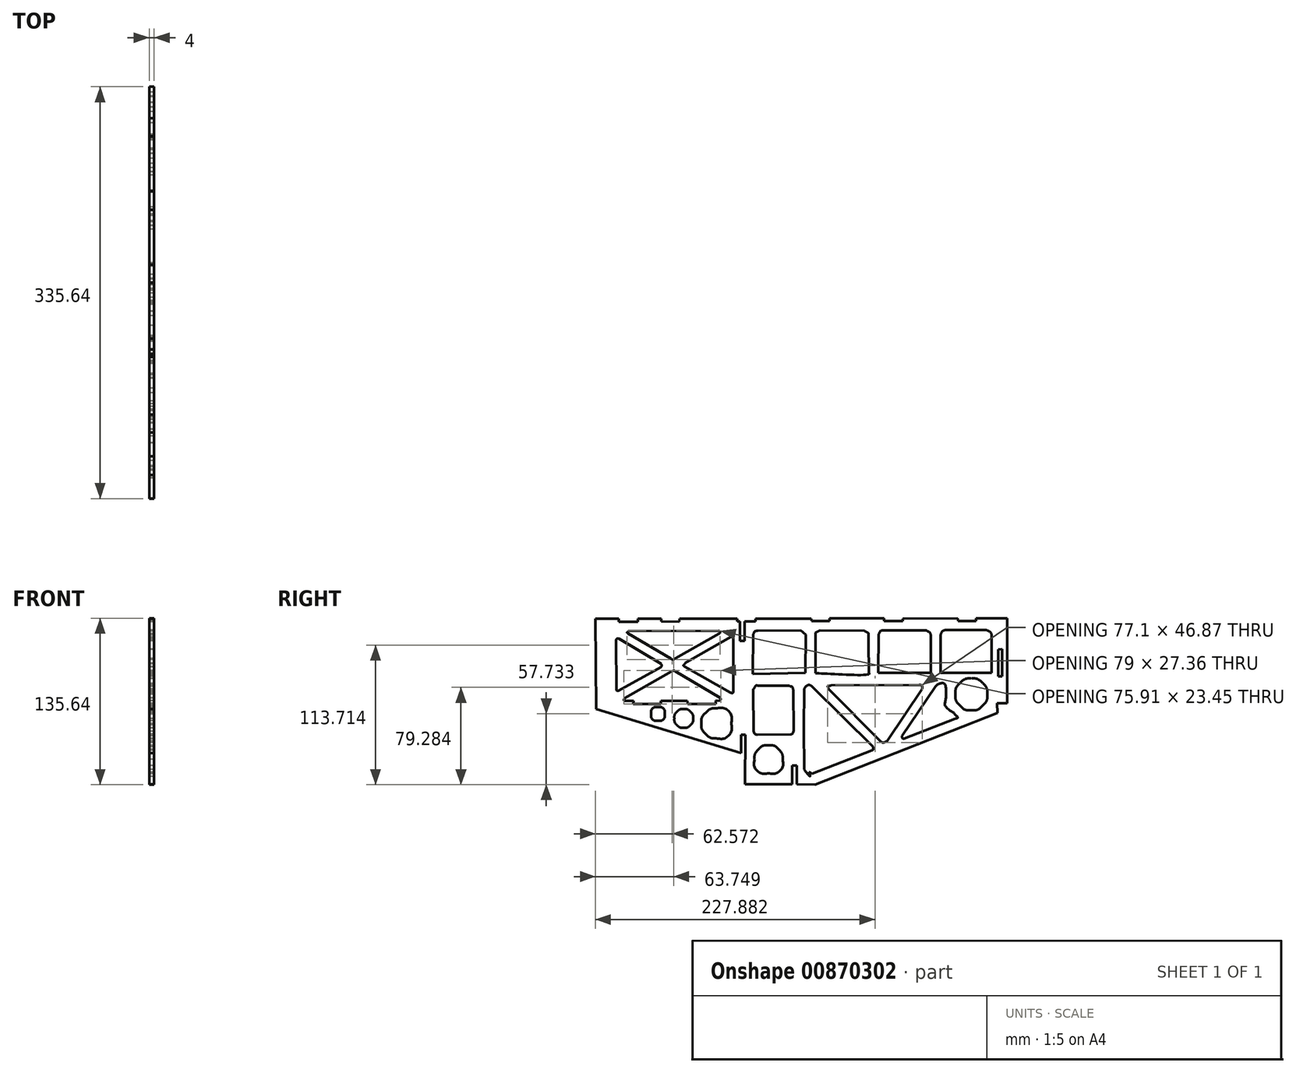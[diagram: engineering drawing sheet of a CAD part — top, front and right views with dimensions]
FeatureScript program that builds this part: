
annotation { "Feature Type Name" : "Feature", "Feature Type Description" : "" }
export const myFeature = defineFeature(function(context is Context, id is Id, definition is map)
    precondition{}
    {
        {
            var Q0;
            Q0=qCreatedBy(makeId("Right.planeOp"),FACE);
            var sketch = newSketch(context, id + "F0", { "sketchPlane" : qUnion([Q0])});
            skLineSegment(sketch, "E0", {"start": v(-35.34, 12.8) * mm, "end": v(-9.65, 12.66) * mm});
            skLineSegment(sketch, "E1", {"start": v(-6.53, 9.34) * mm, "end": v(-6.37, -24.32) * mm});
            skLineSegment(sketch, "E2", {"start": v(-8.68, -26.77) * mm, "end": v(-36.17, -27.13) * mm});
            skLineSegment(sketch, "E3", {"start": v(-38.88, -24.36) * mm, "end": v(-39.35, 9.67) * mm});
            skLineSegment(sketch, "E4", {"start": v(-167.82, 67.26) * mm, "end": v(-148.64, 67.36) * mm});
            skLineSegment(sketch, "E5", {"start": v(-148.64, 67.36) * mm, "end": v(-148.66, 64.78) * mm});
            skLineSegment(sketch, "E6", {"start": v(-148.66, 64.78) * mm, "end": v(-133.38, 64.95) * mm});
            skLineSegment(sketch, "E7", {"start": v(-133.38, 64.95) * mm, "end": v(-133.35, 67.39) * mm});
            skLineSegment(sketch, "E8", {"start": v(-133.35, 67.39) * mm, "end": v(-114.03, 67.41) * mm});
            skLineSegment(sketch, "E9", {"start": v(-114.03, 67.41) * mm, "end": v(-114.18, 65.04) * mm});
            skLineSegment(sketch, "E10", {"start": v(-114.18, 65.04) * mm, "end": v(-99.45, 65) * mm});
            skLineSegment(sketch, "E11", {"start": v(-99.45, 65) * mm, "end": v(-99.35, 67.43) * mm});
            skLineSegment(sketch, "E12", {"start": v(-99.35, 67.43) * mm, "end": v(-52.32, 67.5) * mm});
            skLineSegment(sketch, "E13", {"start": v(-52.32, 67.5) * mm, "end": v(-52.32, 65.13) * mm});
            skLineSegment(sketch, "E14", {"start": v(-52.32, 65.13) * mm, "end": v(-50.06, 65.16) * mm});
            skLineSegment(sketch, "E15", {"start": v(-50.06, 65.16) * mm, "end": v(-50.04, 49.2) * mm});
            skLineSegment(sketch, "E16", {"start": v(-50.04, 49.2) * mm, "end": v(-46.26, 49.2) * mm});
            skLineSegment(sketch, "E17", {"start": v(-46.26, 49.2) * mm, "end": v(-46.26, 65.21) * mm});
            skLineSegment(sketch, "E18", {"start": v(-46.26, 65.21) * mm, "end": v(-37.38, 65.34) * mm});
            skLineSegment(sketch, "E19", {"start": v(-37.38, 65.34) * mm, "end": v(-37.43, 67.48) * mm});
            skLineSegment(sketch, "E20", {"start": v(-37.43, 67.48) * mm, "end": v(8.06, 67.55) * mm});
            skLineSegment(sketch, "E21", {"start": v(8.06, 67.55) * mm, "end": v(8.26, 65.47) * mm});
            skLineSegment(sketch, "E22", {"start": v(8.26, 65.47) * mm, "end": v(22.9, 65.44) * mm});
            skLineSegment(sketch, "E23", {"start": v(22.9, 65.44) * mm, "end": v(23, 67.58) * mm});
            skLineSegment(sketch, "E24", {"start": v(23, 67.58) * mm, "end": v(67.49, 67.65) * mm});
            skLineSegment(sketch, "E25", {"start": v(67.49, 67.65) * mm, "end": v(67.44, 65.38) * mm});
            skLineSegment(sketch, "E26", {"start": v(67.44, 65.38) * mm, "end": v(82.72, 65.5) * mm});
            skLineSegment(sketch, "E27", {"start": v(82.72, 65.5) * mm, "end": v(82.82, 67.53) * mm});
            skLineSegment(sketch, "E28", {"start": v(82.82, 67.53) * mm, "end": v(127.42, 67.68) * mm});
            skLineSegment(sketch, "E29", {"start": v(127.42, 67.68) * mm, "end": v(127.62, 65.56) * mm});
            skLineSegment(sketch, "E30", {"start": v(127.62, 65.56) * mm, "end": v(142.25, 65.54) * mm});
            skLineSegment(sketch, "E31", {"start": v(142.25, 65.54) * mm, "end": v(142.3, 67.74) * mm});
            skLineSegment(sketch, "E32", {"start": v(142.3, 67.74) * mm, "end": v(167.82, 67.82) * mm});
            skLineSegment(sketch, "E33", {"start": v(167.82, 67.82) * mm, "end": v(167.82, -1.63) * mm});
            skLineSegment(sketch, "E34", {"start": v(167.82, -1.63) * mm, "end": v(159.6, -1.35) * mm});
            skLineSegment(sketch, "E35", {"start": v(159.6, -1.35) * mm, "end": v(159.88, -9.57) * mm});
            skLineSegment(sketch, "E36", {"start": v(159.88, -9.57) * mm, "end": v(11.27, -67.82) * mm});
            skLineSegment(sketch, "E37", {"start": v(11.27, -67.82) * mm, "end": v(-3.77, -67.68) * mm});
            skLineSegment(sketch, "E38", {"start": v(-3.77, -67.68) * mm, "end": v(-3.76, -52.35) * mm});
            skLineSegment(sketch, "E39", {"start": v(-3.76, -52.35) * mm, "end": v(-7.49, -52.33) * mm});
            skLineSegment(sketch, "E40", {"start": v(-7.49, -52.33) * mm, "end": v(-7.63, -67.6) * mm});
            skLineSegment(sketch, "E41", {"start": v(-7.63, -67.6) * mm, "end": v(-45.92, -67.68) * mm});
            skLineSegment(sketch, "E42", {"start": v(-45.92, -67.68) * mm, "end": v(-45.64, -27.14) * mm});
            skLineSegment(sketch, "E43", {"start": v(-45.64, -27.14) * mm, "end": v(-49.04, -27.14) * mm});
            skLineSegment(sketch, "E44", {"start": v(-49.04, -27.14) * mm, "end": v(-49.04, -42.17) * mm});
            skLineSegment(sketch, "E45", {"start": v(-49.04, -42.17) * mm, "end": v(-167.25, -6.17) * mm});
            skLineSegment(sketch, "E46", {"start": v(-167.25, -6.17) * mm, "end": v(-167.82, 67.26) * mm});
            skLineSegment(sketch, "E47", {"start": v(-140.96, 57.3) * mm, "end": v(-67.1, 57.62) * mm});
            skLineSegment(sketch, "E48", {"start": v(-66.89, 55.38) * mm, "end": v(-102.87, 34.97) * mm});
            skLineSegment(sketch, "E49", {"start": v(-106.46, 34.95) * mm, "end": v(-141.33, 55.29) * mm});
            skLineSegment(sketch, "E50", {"start": v(-140.96, 57.3) * mm, "end": v(-140.96, 57.3) * mm});
            skLineSegment(sketch, "E51", {"start": v(-94.85, 31.14) * mm, "end": v(-57.55, 52.48) * mm});
            skLineSegment(sketch, "E52", {"start": v(-55.38, 51.31) * mm, "end": v(-55.44, 8.2) * mm});
            skLineSegment(sketch, "E53", {"start": v(-57.81, 6.93) * mm, "end": v(-95.2, 28.46) * mm});
            skLineSegment(sketch, "E54", {"start": v(-102.8, 24.6) * mm, "end": v(-66.15, 2.96) * mm});
            skLineSegment(sketch, "E55", {"start": v(-67.02, 0.55) * mm, "end": v(-69.9, 0.58) * mm});
            skLineSegment(sketch, "E56", {"start": v(-69.9, 0.58) * mm, "end": v(-69.86, -2.02) * mm});
            skLineSegment(sketch, "E57", {"start": v(-69.86, -2.02) * mm, "end": v(-92.66, -2.05) * mm});
            skLineSegment(sketch, "E58", {"start": v(-92.66, -2.05) * mm, "end": v(-92.83, 0.56) * mm});
            skLineSegment(sketch, "E59", {"start": v(-92.83, 0.56) * mm, "end": v(-114.44, 0.44) * mm});
            skLineSegment(sketch, "E60", {"start": v(-114.44, 0.44) * mm, "end": v(-114.48, -2.15) * mm});
            skLineSegment(sketch, "E61", {"start": v(-114.48, -2.15) * mm, "end": v(-136.93, -2.21) * mm});
            skLineSegment(sketch, "E62", {"start": v(-136.93, -2.21) * mm, "end": v(-136.82, 0.35) * mm});
            skLineSegment(sketch, "E63", {"start": v(-136.82, 0.35) * mm, "end": v(-143.8, 0.35) * mm});
            skLineSegment(sketch, "E64", {"start": v(-144.07, 2.52) * mm, "end": v(-105.61, 24.62) * mm});
            skLineSegment(sketch, "E65", {"start": v(-102.8, 24.6) * mm, "end": v(-102.8, 24.6) * mm});
            skLineSegment(sketch, "E66", {"start": v(-151.08, 49.68) * mm, "end": v(-150.86, 9.73) * mm});
            skLineSegment(sketch, "E67", {"start": v(-148.95, 8.56) * mm, "end": v(-114.29, 28.13) * mm});
            skLineSegment(sketch, "E68", {"start": v(-114.32, 30.7) * mm, "end": v(-148.8, 51.1) * mm});
            skLineSegment(sketch, "E69", {"start": v(-39.68, 22.48) * mm, "end": v(3.4, 23.32) * mm});
            skLineSegment(sketch, "E70", {"start": v(3.4, 23.32) * mm, "end": v(3.62, 54.46) * mm});
            skLineSegment(sketch, "E71", {"start": v(3.62, 54.46) * mm, "end": v(-0.4, 57.86) * mm});
            skLineSegment(sketch, "E72", {"start": v(-0.4, 57.86) * mm, "end": v(-35.54, 57.55) * mm});
            skLineSegment(sketch, "E73", {"start": v(-39.16, 54.7) * mm, "end": v(-39.68, 22.48) * mm});
            skLineSegment(sketch, "E74", {"start": v(11.5, 54.63) * mm, "end": v(11.63, 23.04) * mm});
            skLineSegment(sketch, "E75", {"start": v(51.66, 57.5) * mm, "end": v(15.06, 57.76) * mm});
            skLineSegment(sketch, "E76", {"start": v(62.96, 54.57) * mm, "end": v(62.8, 23.32) * mm});
            skLineSegment(sketch, "E77", {"start": v(62.8, 23.32) * mm, "end": v(105.38, 23.4) * mm});
            skLineSegment(sketch, "E78", {"start": v(105.38, 23.4) * mm, "end": v(105.49, 53.98) * mm});
            skLineSegment(sketch, "E79", {"start": v(102.03, 57.82) * mm, "end": v(66.65, 57.83) * mm});
            skLineSegment(sketch, "E80", {"start": v(117, 58.05) * mm, "end": v(151.01, 58.04) * mm});
            skLineSegment(sketch, "E81", {"start": v(155, 54.07) * mm, "end": v(155.21, 23.25) * mm});
            skLineSegment(sketch, "E82", {"start": v(155.21, 23.25) * mm, "end": v(113.4, 23.25) * mm});
            skLineSegment(sketch, "E83", {"start": v(113.4, 23.25) * mm, "end": v(113.6, 54.45) * mm});
            skLineSegment(sketch, "E84", {"start": v(109.43, 12.3) * mm, "end": v(82.13, -28.04) * mm});
            skLineSegment(sketch, "E85", {"start": v(83.67, -30.34) * mm, "end": v(125.16, -14.2) * mm});
            skLineSegment(sketch, "E86", {"start": v(160.44, 42.32) * mm, "end": v(163.63, 42.53) * mm});
            skLineSegment(sketch, "E87", {"start": v(163.63, 42.53) * mm, "end": v(163.5, 20.27) * mm});
            skLineSegment(sketch, "E88", {"start": v(163.5, 20.27) * mm, "end": v(160.45, 20.33) * mm});
            skLineSegment(sketch, "E89", {"start": v(160.45, 20.33) * mm, "end": v(160.44, 42.32) * mm});
            skLineSegment(sketch, "E90", {"start": v(24.48, 13.03) * mm, "end": v(95.92, 13.32) * mm});
            skLineSegment(sketch, "E91", {"start": v(98.38, 10.3) * mm, "end": v(69.94, -32.3) * mm});
            skLineSegment(sketch, "E92", {"start": v(64.18, -32.25) * mm, "end": v(22.67, 9.59) * mm});
            skLineSegment(sketch, "E93", {"start": v(8.6, 12.2) * mm, "end": v(58.54, -37.15) * mm});
            skLineSegment(sketch, "E94", {"start": v(57.67, -40.01) * mm, "end": v(8.58, -59.05) * mm});
            skLineSegment(sketch, "E95", {"start": v(2.21, -55.54) * mm, "end": v(1.94, -21.7) * mm});
            skLineSegment(sketch, "E96", {"start": v(1.94, -21.7) * mm, "end": v(2.26, 9.95) * mm});
            skFitSpline(sketch, "E97", {"points": [v(-9.65, 12.66) * mm, v(-8.65, 12.04) * mm, v(-7.7, 12.08) * mm, v(-6.53, 9.34) * mm]});
            skFitSpline(sketch, "E98", {"points": [v(-6.37, -24.32) * mm, v(-6.77, -25.51) * mm, v(-7.39, -26.52) * mm, v(-8.68, -26.77) * mm]});
            skFitSpline(sketch, "E99", {"points": [v(-36.17, -27.13) * mm, v(-37.8, -26.6) * mm, v(-38.46, -25.54) * mm, v(-38.88, -24.36) * mm]});
            skFitSpline(sketch, "E100", {"points": [v(-39.35, 9.67) * mm, v(-38.18, 11.2) * mm, v(-37.05, 12.9) * mm, v(-35.34, 12.8) * mm]});
            skFitSpline(sketch, "E101", {"points": [v(-67.1, 57.62) * mm, v(-66.58, 56.92) * mm, v(-66.12, 56.21) * mm, v(-66.89, 55.38) * mm]});
            skFitSpline(sketch, "E102", {"points": [v(-102.87, 34.97) * mm, v(-103.76, 34.34) * mm, v(-105.56, 34.27) * mm, v(-106.46, 34.95) * mm]});
            skFitSpline(sketch, "E103", {"points": [v(-141.33, 55.29) * mm, v(-142.03, 56.2) * mm, v(-141.57, 56.78) * mm, v(-140.96, 57.3) * mm]});
            skFitSpline(sketch, "E104", {"points": [v(-95.2, 28.46) * mm, v(-96.1, 29.46) * mm, v(-95.1, 30.4) * mm, v(-94.85, 31.14) * mm]});
            skFitSpline(sketch, "E105", {"points": [v(-57.55, 52.48) * mm, v(-56.71, 52.35) * mm, v(-55.72, 52.56) * mm, v(-55.38, 51.31) * mm]});
            skFitSpline(sketch, "E106", {"points": [v(-55.44, 8.2) * mm, v(-55.96, 6.75) * mm, v(-56.92, 6.9) * mm, v(-57.81, 6.93) * mm]});
            skFitSpline(sketch, "E107", {"points": [v(-66.15, 2.96) * mm, v(-65.76, 1.6) * mm, v(-66.3, 1) * mm, v(-67.02, 0.55) * mm]});
            skFitSpline(sketch, "E108", {"points": [v(-143.8, 0.35) * mm, v(-144.74, 1.02) * mm, v(-144.5, 1.76) * mm, v(-144.07, 2.52) * mm]});
            skFitSpline(sketch, "E109", {"points": [v(-105.61, 24.62) * mm, v(-104.72, 24.84) * mm, v(-103.83, 25.14) * mm, v(-102.8, 24.6) * mm]});
            skFitSpline(sketch, "E110", {"points": [v(-148.8, 51.1) * mm, v(-149.67, 51.18) * mm, v(-150.49, 51) * mm, v(-151.08, 49.68) * mm]});
            skFitSpline(sketch, "E111", {"points": [v(-150.86, 9.73) * mm, v(-150.55, 8.85) * mm, v(-149.79, 8.65) * mm, v(-148.95, 8.56) * mm]});
            skFitSpline(sketch, "E112", {"points": [v(-114.29, 28.13) * mm, v(-113.8, 28.94) * mm, v(-114.04, 29.88) * mm, v(-114.32, 30.7) * mm]});
            skFitSpline(sketch, "E113", {"points": [v(-35.54, 57.55) * mm, v(-38.13, 56.94) * mm, v(-38.64, 55.82) * mm, v(-39.16, 54.7) * mm]});
            skFitSpline(sketch, "E114", {"points": [v(15.06, 57.76) * mm, v(13.27, 56.92) * mm, v(11.64, 56.03) * mm, v(11.5, 54.63) * mm]});
            skFitSpline(sketch, "E115", {"points": [v(11.63, 23.04) * mm, v(11.63, 23.04) * mm, v(11.63, 23.04) * mm, v(12.19, 23.03) * mm, v(55, 22.2) * mm, v(55, 23.32) * mm]});
            skFitSpline(sketch, "E116", {"points": [v(55, 23.32) * mm, v(55, 24.44) * mm, v(54.7, 53.58) * mm, v(54.7, 53.97) * mm, v(54.7, 53.97) * mm, v(54.7, 53.97) * mm]});
            skFitSpline(sketch, "E117", {"points": [v(54.7, 53.97) * mm, v(54.6, 55.67) * mm, v(53, 56.5) * mm, v(51.66, 57.5) * mm]});
            skFitSpline(sketch, "E118", {"points": [v(66.65, 57.83) * mm, v(64.46, 57.35) * mm, v(63.69, 55.97) * mm, v(62.96, 54.57) * mm]});
            skFitSpline(sketch, "E119", {"points": [v(105.49, 53.98) * mm, v(104.43, 56.48) * mm, v(103.22, 56.94) * mm, v(102.03, 57.82) * mm]});
            skFitSpline(sketch, "E120", {"points": [v(151.01, 58.04) * mm, v(152.7, 57.3) * mm, v(154.43, 56.06) * mm, v(155, 54.07) * mm]});
            skFitSpline(sketch, "E121", {"points": [v(113.6, 54.45) * mm, v(114.1, 55.92) * mm, v(115.06, 57.26) * mm, v(117, 58.05) * mm]});
            skFitSpline(sketch, "E122", {"points": [v(117.9, 10.37) * mm, v(116.34, 14.66) * mm, v(111.61, 14.1) * mm, v(109.43, 12.3) * mm]});
            skFitSpline(sketch, "E123", {"points": [v(82.13, -28.04) * mm, v(82.15, -29.24) * mm, v(82.46, -30.18) * mm, v(83.67, -30.34) * mm]});
            skFitSpline(sketch, "E124", {"points": [v(125.16, -14.2) * mm, v(127.52, -13.19) * mm, v(126.17, -11.6) * mm, v(124.47, -9.55) * mm]});
            skFitSpline(sketch, "E125", {"points": [v(124.47, -9.55) * mm, v(117.17, -3.29) * mm, v(117.75, 2.2) * mm, v(117.9, 10.37) * mm]});
            skFitSpline(sketch, "E126", {"points": [v(95.92, 13.32) * mm, v(97.79, 13.16) * mm, v(98.57, 12.13) * mm, v(98.38, 10.3) * mm]});
            skFitSpline(sketch, "E127", {"points": [v(69.94, -32.3) * mm, v(68.14, -33.18) * mm, v(66.26, -33.5) * mm, v(64.18, -32.25) * mm]});
            skFitSpline(sketch, "E128", {"points": [v(22.67, 9.59) * mm, v(21.56, 12.44) * mm, v(22.76, 12.65) * mm, v(24.48, 13.03) * mm]});
            skFitSpline(sketch, "E129", {"points": [v(58.54, -37.15) * mm, v(58.45, -38.1) * mm, v(58.64, -39.06) * mm, v(57.67, -40.01) * mm]});
            skFitSpline(sketch, "E130", {"points": [v(8.58, -59.05) * mm, v(6.48, -57.9) * mm, v(7.15, -61) * mm, v(2.21, -55.54) * mm]});
            skFitSpline(sketch, "E131", {"points": [v(2.26, 9.95) * mm, v(3.32, 11.73) * mm, v(5.93, 13.34) * mm, v(8.6, 12.2) * mm]});
            skFitSpline(sketch, "E132", {"points": [v(-111.45, -10.22) * mm, v(-111.45, -13.23) * mm, v(-113.9, -15.67) * mm, v(-116.9, -15.67) * mm]});
            skFitSpline(sketch, "E133", {"points": [v(-116.9, -15.67) * mm, v(-119.9, -15.67) * mm, v(-122.34, -13.23) * mm, v(-122.34, -10.22) * mm]});
            skFitSpline(sketch, "E134", {"points": [v(-122.34, -10.22) * mm, v(-122.34, -7.22) * mm, v(-119.9, -4.78) * mm, v(-116.9, -4.78) * mm]});
            skFitSpline(sketch, "E135", {"points": [v(-116.9, -4.78) * mm, v(-113.9, -4.78) * mm, v(-111.45, -7.22) * mm, v(-111.45, -10.22) * mm]});
            skFitSpline(sketch, "E136", {"points": [v(-88.16, -13.87) * mm, v(-88.16, -15.9) * mm, v(-88.97, -17.86) * mm, v(-90.41, -19.3) * mm]});
            skFitSpline(sketch, "E137", {"points": [v(-90.41, -19.3) * mm, v(-91.85, -20.74) * mm, v(-93.8, -21.55) * mm, v(-95.85, -21.55) * mm]});
            skFitSpline(sketch, "E138", {"points": [v(-95.85, -21.55) * mm, v(-97.88, -21.55) * mm, v(-99.84, -20.74) * mm, v(-101.28, -19.3) * mm]});
            skFitSpline(sketch, "E139", {"points": [v(-101.28, -19.3) * mm, v(-102.72, -17.86) * mm, v(-103.53, -15.9) * mm, v(-103.53, -13.87) * mm]});
            skFitSpline(sketch, "E140", {"points": [v(-103.53, -13.87) * mm, v(-103.53, -11.83) * mm, v(-102.72, -9.88) * mm, v(-101.28, -8.44) * mm]});
            skFitSpline(sketch, "E141", {"points": [v(-101.28, -8.44) * mm, v(-99.84, -7) * mm, v(-97.88, -6.19) * mm, v(-95.85, -6.19) * mm]});
            skFitSpline(sketch, "E142", {"points": [v(-95.85, -6.19) * mm, v(-93.8, -6.19) * mm, v(-91.85, -7) * mm, v(-90.41, -8.44) * mm]});
            skFitSpline(sketch, "E143", {"points": [v(-90.41, -8.44) * mm, v(-88.97, -9.88) * mm, v(-88.16, -11.83) * mm, v(-88.16, -13.87) * mm]});
            skFitSpline(sketch, "E144", {"points": [v(-57.13, -17.93) * mm, v(-57.13, -24.66) * mm, v(-62.59, -30.1) * mm, v(-69.32, -30.1) * mm]});
            skFitSpline(sketch, "E145", {"points": [v(-69.32, -30.1) * mm, v(-72.55, -30.1) * mm, v(-75.64, -28.83) * mm, v(-77.93, -26.54) * mm]});
            skFitSpline(sketch, "E146", {"points": [v(-77.93, -26.54) * mm, v(-80.21, -24.26) * mm, v(-81.5, -21.16) * mm, v(-81.5, -17.93) * mm]});
            skFitSpline(sketch, "E147", {"points": [v(-81.5, -17.93) * mm, v(-81.5, -14.7) * mm, v(-80.21, -11.6) * mm, v(-77.93, -9.31) * mm]});
            skFitSpline(sketch, "E148", {"points": [v(-77.93, -9.31) * mm, v(-75.64, -7.03) * mm, v(-72.55, -5.75) * mm, v(-69.32, -5.75) * mm]});
            skFitSpline(sketch, "E149", {"points": [v(-69.32, -5.75) * mm, v(-62.59, -5.75) * mm, v(-57.13, -11.2) * mm, v(-57.13, -17.93) * mm]});
            skFitSpline(sketch, "E150", {"points": [v(-15.27, -47.16) * mm, v(-15.27, -53.48) * mm, v(-20.4, -58.6) * mm, v(-26.7, -58.6) * mm]});
            skFitSpline(sketch, "E151", {"points": [v(-26.7, -58.6) * mm, v(-33.03, -58.6) * mm, v(-38.15, -53.48) * mm, v(-38.15, -47.16) * mm]});
            skFitSpline(sketch, "E152", {"points": [v(-38.15, -47.16) * mm, v(-38.15, -44.13) * mm, v(-36.94, -41.22) * mm, v(-34.8, -39.07) * mm]});
            skFitSpline(sketch, "E153", {"points": [v(-34.8, -39.07) * mm, v(-32.65, -36.93) * mm, v(-29.74, -35.72) * mm, v(-26.7, -35.72) * mm]});
            skFitSpline(sketch, "E154", {"points": [v(-26.7, -35.72) * mm, v(-23.67, -35.72) * mm, v(-20.77, -36.93) * mm, v(-18.62, -39.07) * mm]});
            skFitSpline(sketch, "E155", {"points": [v(-18.62, -39.07) * mm, v(-16.48, -41.22) * mm, v(-15.27, -44.13) * mm, v(-15.27, -47.16) * mm]});
            skFitSpline(sketch, "E156", {"points": [v(151.49, 5.7) * mm, v(151.49, 2.26) * mm, v(150.12, -1.03) * mm, v(147.7, -3.46) * mm]});
            skFitSpline(sketch, "E157", {"points": [v(147.7, -3.46) * mm, v(145.27, -5.89) * mm, v(141.97, -7.25) * mm, v(138.54, -7.25) * mm]});
            skFitSpline(sketch, "E158", {"points": [v(138.54, -7.25) * mm, v(135.1, -7.25) * mm, v(131.82, -5.89) * mm, v(129.39, -3.46) * mm]});
            skFitSpline(sketch, "E159", {"points": [v(129.39, -3.46) * mm, v(126.96, -1.03) * mm, v(125.6, 2.26) * mm, v(125.6, 5.7) * mm]});
            skFitSpline(sketch, "E160", {"points": [v(125.6, 5.7) * mm, v(125.6, 9.13) * mm, v(126.96, 12.42) * mm, v(129.39, 14.85) * mm]});
            skFitSpline(sketch, "E161", {"points": [v(129.39, 14.85) * mm, v(131.82, 17.28) * mm, v(135.1, 18.64) * mm, v(138.54, 18.64) * mm]});
            skFitSpline(sketch, "E162", {"points": [v(138.54, 18.64) * mm, v(141.97, 18.64) * mm, v(145.27, 17.28) * mm, v(147.7, 14.85) * mm]});
            skFitSpline(sketch, "E163", {"points": [v(147.7, 14.85) * mm, v(150.12, 12.42) * mm, v(151.49, 9.13) * mm, v(151.49, 5.7) * mm]});
            skSolve(sketch);
        }
        {
            var Q0;
            Q0 = qSketchRegion(id + "F0", true);
            extrude(context, id + "F1", {"entities" : qUnion([Q0]), "depth" : 4 * mm, "offsetDistance" : 25 * mm});
        }
    });
